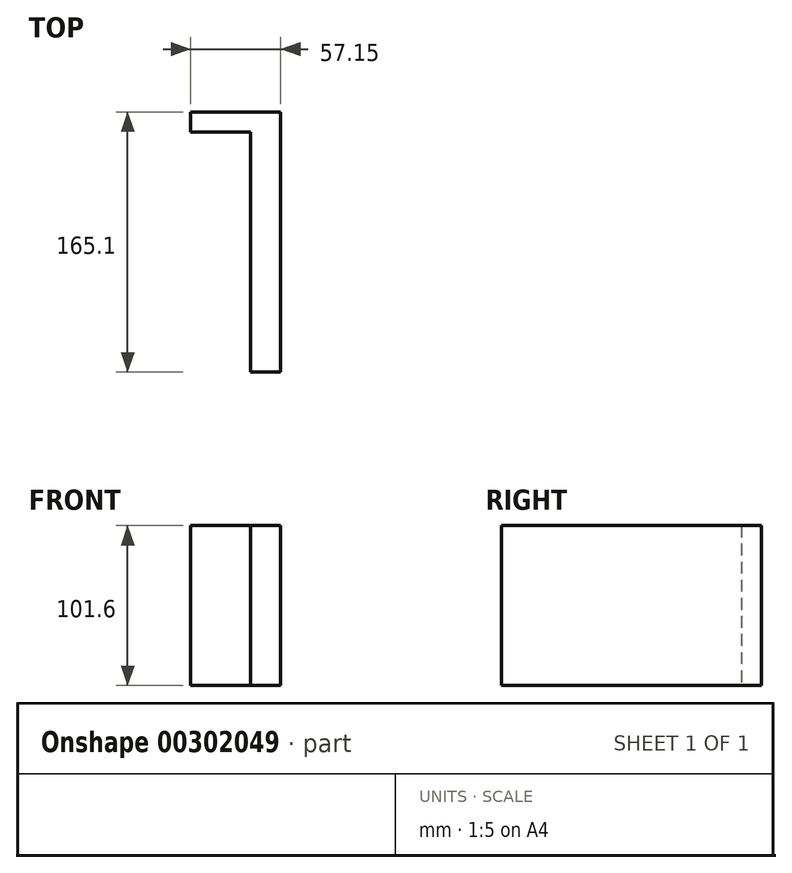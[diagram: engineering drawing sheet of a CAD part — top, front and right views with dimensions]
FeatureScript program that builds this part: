
annotation { "Feature Type Name" : "Feature", "Feature Type Description" : "" }
export const myFeature = defineFeature(function(context is Context, id is Id, definition is map)
    precondition{}
    {
        {
            var Q0;
            Q0=qCreatedBy(makeId("Top.planeOp"),FACE);
            var sketch = newSketch(context, id + "F0", { "sketchPlane" : qUnion([Q0])});
            skLineSegment(sketch, "E0", {"start": v(0, 0) * mm, "end": v(-38.1, 0) * mm});
            skLineSegment(sketch, "E1", {"start": v(-38.1, 0) * mm, "end": v(-38.1, 12.7) * mm});
            skLineSegment(sketch, "E2", {"start": v(-38.1, 12.7) * mm, "end": v(19.05, 12.7) * mm});
            skLineSegment(sketch, "E3", {"start": v(19.05, 12.7) * mm, "end": v(19.05, -152.4) * mm});
            skLineSegment(sketch, "E4", {"start": v(19.05, -152.4) * mm, "end": v(0, -152.4) * mm});
            skLineSegment(sketch, "E5", {"start": v(0, -152.4) * mm, "end": v(0, 0) * mm});
            skSolve(sketch);
        }
        {
            var Q0;
            Q0 = qSketchRegion(id + "F0", true);
            extrude(context, id + "F1", {"entities" : qUnion([Q0]), "depth" : 101.6 * mm});
        }
    });
